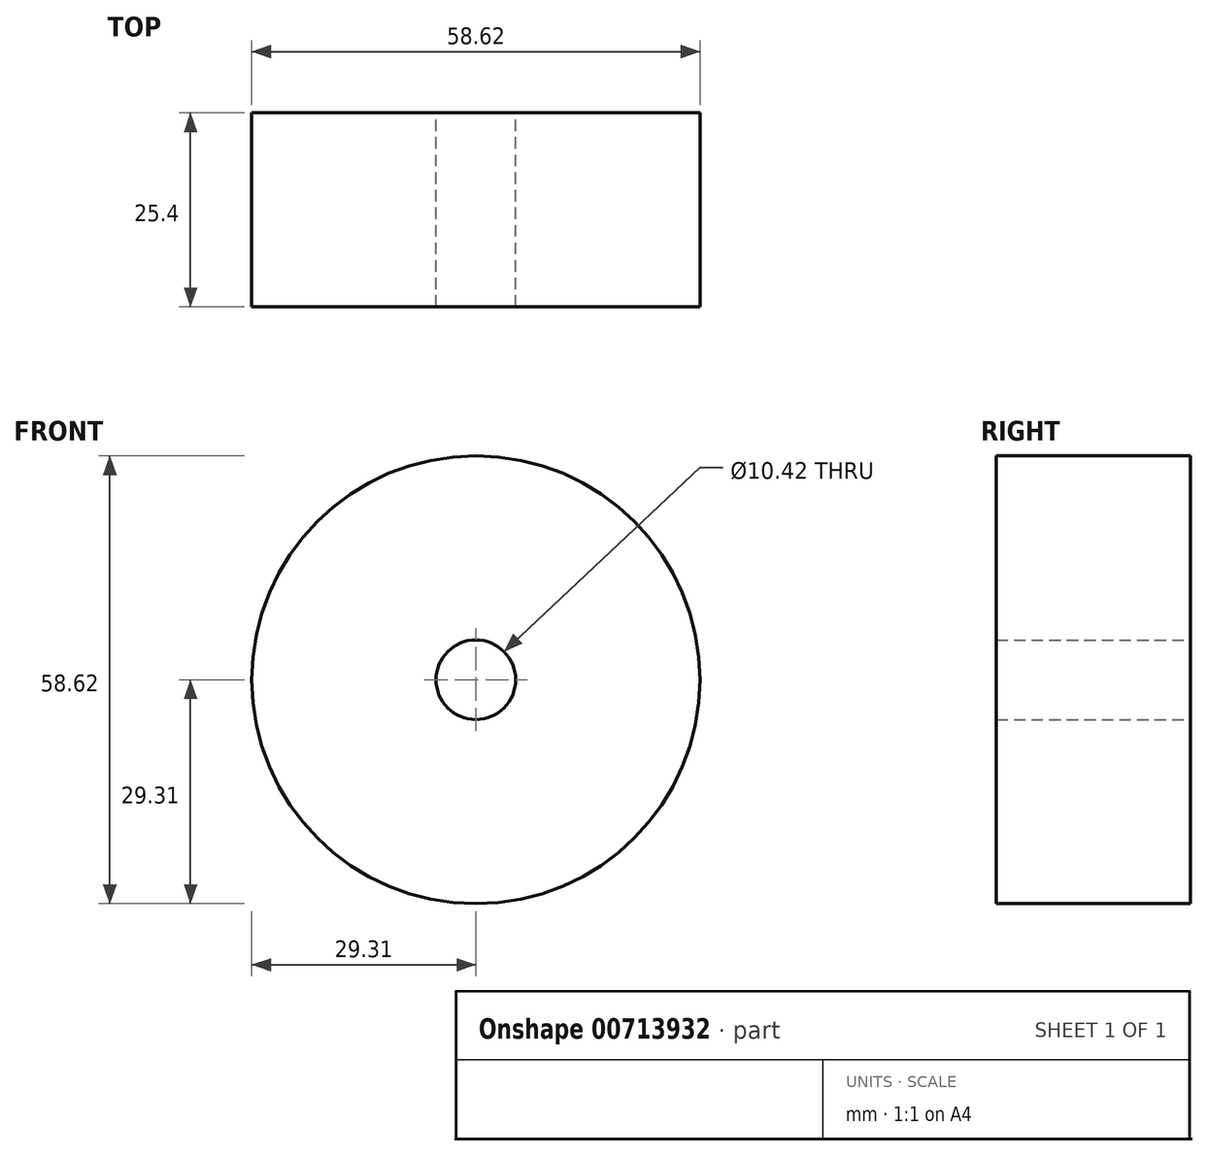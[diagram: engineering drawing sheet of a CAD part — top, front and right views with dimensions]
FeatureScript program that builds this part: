
annotation { "Feature Type Name" : "Feature", "Feature Type Description" : "" }
export const myFeature = defineFeature(function(context is Context, id is Id, definition is map)
    precondition{}
    {
        {
            var Q0;
            Q0=qCreatedBy(makeId("Front.planeOp"),FACE);
            var sketch = newSketch(context, id + "F0", { "sketchPlane" : qUnion([Q0])});
            skCircle(sketch, "E0", {"center": v(0, 0) * mm, "radius": 29.3 * mm});
            skCircle(sketch, "E1", {"center": v(0, 0) * mm, "radius": 5.2 * mm});
            skSolve(sketch);
        }
        {
            var Q0;
            Q0=makeQuery(id+"F0.imprint","IMPRINT",FACE,{"disambiguationData":[TD([[makeQuery(id+"F0.imprint","IMPRINT",EDGE,{"derivedFrom":sQuery(id+"F0.wireOp",EDGE,"E0")}),1.0]])]});
            var sketch = newSketch(context, id + "F1", { "sketchPlane" : qUnion([Q0])});
            skSolve(sketch);
        }
        {
            var Q0;
            Q0=makeQuery(id+"F1.imprint","IMPRINT",FACE,{"disambiguationData":[TD([[makeQuery(id+"F1.imprint","IMPRINT",EDGE,{"derivedFrom":makeQuery(id+"F0.imprint","IMPRINT",EDGE,{"derivedFrom":sQuery(id+"F0.wireOp",EDGE,"E0")})}),1.0]])]});
            extrude(context, id + "F2", {"entities" : qUnion([Q0]), "depth" : 25.4 * mm, "offsetDistance" : 25.4 * mm});
        }
    });
